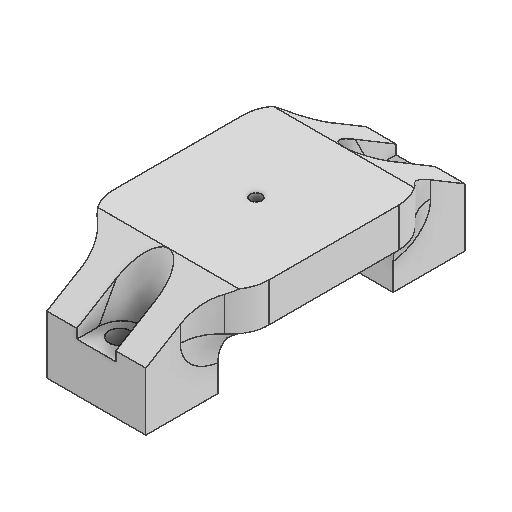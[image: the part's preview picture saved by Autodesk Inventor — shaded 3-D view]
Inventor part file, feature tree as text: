
AUTODESK INVENTOR PART (.ipt)
format: ipt  version: 2025 (Build 290162000, 162)  size: 358,912 bytes
history: native  units: mm
features: projected_geometry x11, extrude x8, sketch x8, fillet x6, plane x2
ambient origin geometry x8: Origin, YZ Plane, XZ Plane, XY Plane, X Axis, Y Axis, Z Axis, Center Point
bodies: Solid1 (feature_tree)
feature tree (35):
  extrude  "Extrusion1"  Depth=40.0mm
  extrude  "Extrusion2"  Depth=10.0mm
  extrude  "Extrusion3"  TaperAngle=0.0deg  [1 undecoded]
  plane  "Work Plane1"
  extrude  "Extrusion4"  TaperAngle=0.0deg  [1 undecoded]
  fillet  "Fillet1"  Radius=10.0mm
  extrude  "Extrusion5"  Depth=10.0mm
  fillet  "Fillet2"  Radius=5.5mm
  extrude  "Extrusion6"  Depth=10.0mm
  fillet  "Fillet3"  Radius=10.0mm
  plane  "Work Plane2"
  fillet  "Fillet4"  [1 undecoded]
  fillet  "Fillet5"  Radius=10.0mm
  fillet  "Fillet6"  Radius=10.0mm
  extrude  "Extrusion7"  Depth=5.0mm
  extrude  "Extrusion8"  Depth=4.0mm
  sketch  "Sketch1"  dims[d0=40.0mm d1=90.0mm]
  sketch  "Sketch2"  dims[d2=10.0mm d3=0.0mm d4=45.0mm]
  projected_geometry  "Projected Loop1"
  sketch  "Sketch3"  dims[d5=25.4mm d6=0.0mm d7=0.0mm]
  projected_geometry  "Projected Loop2"
  sketch  "Sketch4"  dims[d8=16.0mm d9=0.0mm d10=0.0mm d11=0.0mm d12=10.0mm d13=0.0mm]
  projected_geometry  "Projected Loop3"
  projected_geometry  "Projected Loop4"
  sketch  "Sketch5"  dims[d14=2.5mm d15=10.0mm d16=5.5mm]
  projected_geometry  "Projected Loop5"
  projected_geometry  "Projected Loop6"
  sketch  "Sketch6"  dims[d17=5.5mm d18=10.0mm d19=10.0mm d20=0.0mm d21=0.0mm d22=10.0mm d23=10.0mm]
  projected_geometry  "Projected Loop7"
  projected_geometry  "Projected Loop8"
  sketch  "Sketch7"  dims[d24=2.5mm d25=5.0mm]
  projected_geometry  "Projected Loop9"
  projected_geometry  "Projected Loop10"
  sketch  "Sketch8"  dims[d26=4.0mm d27=4.0mm d28=0.0mm d29=0.0mm d30=3.0mm d31=0.0mm d32=0.0mm]
  projected_geometry  "Projected Loop11"
note: 3 required parameter values undecoded (feature->parameter linkage not recoverable at this tier; creation-order binding heuristic only, values carry confidence <= 0.55)
